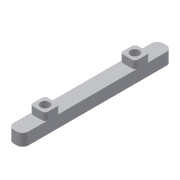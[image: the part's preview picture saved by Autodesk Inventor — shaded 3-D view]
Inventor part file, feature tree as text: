
AUTODESK INVENTOR PART (.ipt)
format: ipt  version: 2013 (Build 170138000, 138)  size: 123,392 bytes
history: native  units: mm
features: extrude x2, hole x2, sketch x2
ambient origin geometry x8: Origin, YZ Plane, XZ Plane, XY Plane, X Axis, Y Axis, Z Axis, Center Point
bodies: Volumenkörper1 (feature_tree)
feature tree (6):
  extrude  "Extrusion1"  Depth=50.0mm
  extrude  "Extrusion2"  Depth=4.0mm TaperAngle=0.0deg
  hole  "Bohrung2"  [1 undecoded]
  hole  "Bohrung3"  [1 undecoded]
  sketch  "Skizze1"  dims[d0=5.0mm d1=50.0mm]
  sketch  "Skizze2"  dims[d2=2.0mm d3=4.0mm d4=0.0mm d10=2.5mm d11=0.0mm d12=1.0mm d13=7.5mm d14=5.0mm d15=5.0mm d16=7.5mm d26=2.5mm d27=2.5mm d28=3.0mm d29=6.0mm d30=4.0mm d31=2.0mm d32=90.0deg d33=8.0mm d34=20.594885mm d35=2.5mm d36=2.5mm d37=3.0mm d38=6.0mm d39=4.0mm d40=2.0mm d41=90.0deg d42=8.0mm d43=20.594885mm]
note: 2 required parameter values undecoded (feature->parameter linkage not recoverable at this tier; creation-order binding heuristic only, values carry confidence <= 0.55)
